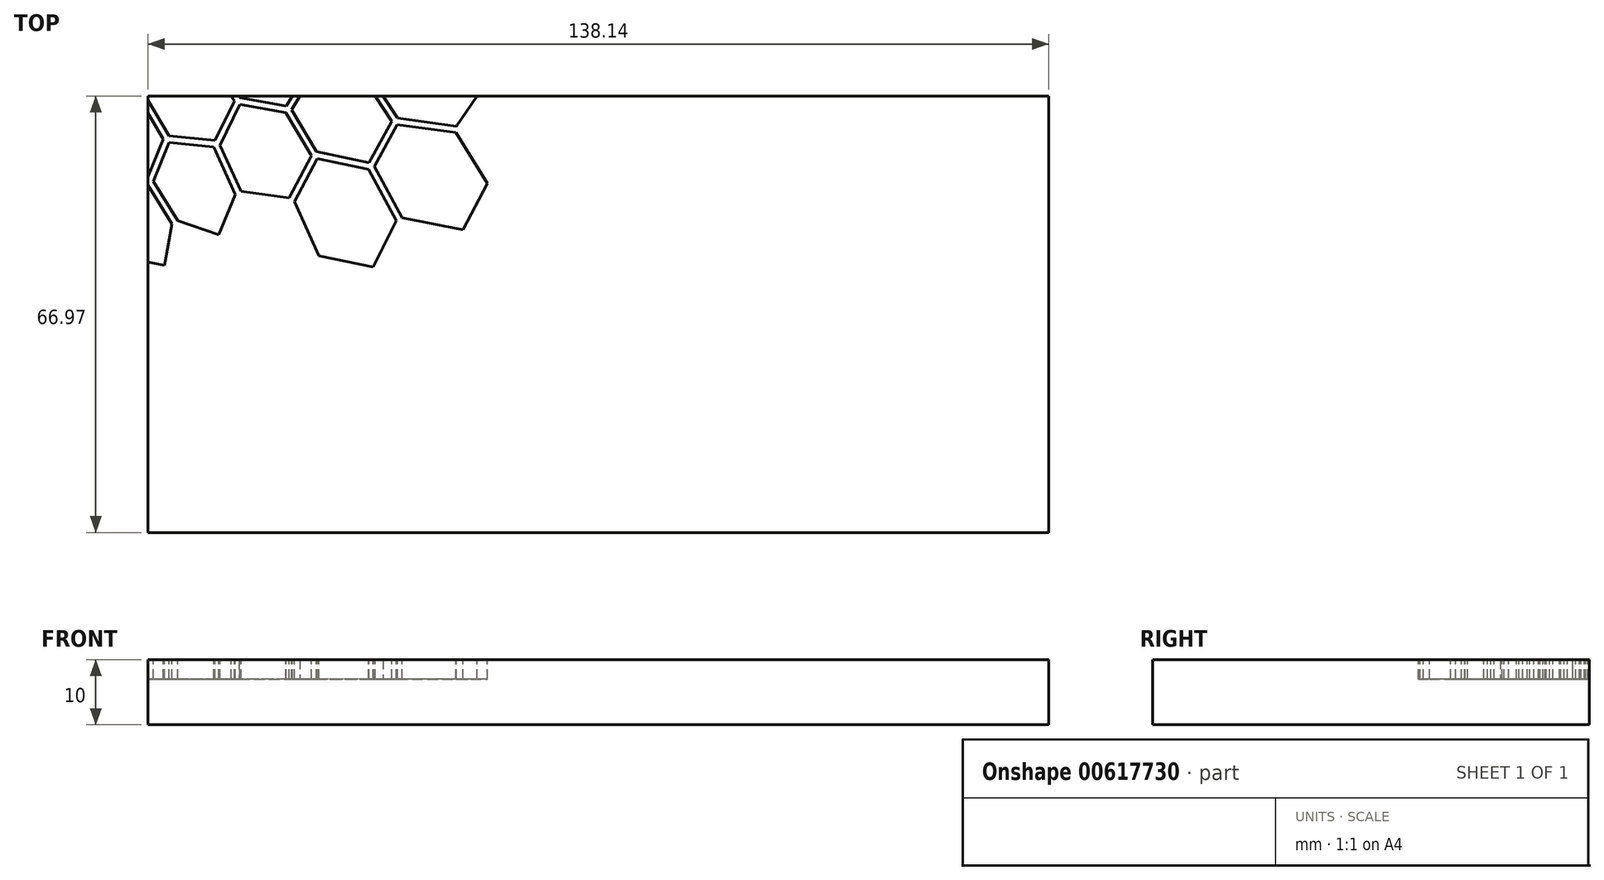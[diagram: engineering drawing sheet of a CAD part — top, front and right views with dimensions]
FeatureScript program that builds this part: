
annotation { "Feature Type Name" : "Feature", "Feature Type Description" : "" }
export const myFeature = defineFeature(function(context is Context, id is Id, definition is map)
    precondition{}
    {
        {
            var Q0;
            Q0=qCreatedBy(makeId("Top.planeOp"),FACE);
            var sketch = newSketch(context, id + "F0", { "sketchPlane" : qUnion([Q0])});
            skLineSegment(sketch, "E0.bottom", {"start": v(-69.07, 33.48) * mm, "end": v(69.07, 33.48) * mm});
            skLineSegment(sketch, "E0.top", {"start": v(-69.07, -33.48) * mm, "end": v(69.07, -33.48) * mm});
            skLineSegment(sketch, "E0.left", {"start": v(-69.07, 33.48) * mm, "end": v(-69.07, -33.48) * mm});
            skLineSegment(sketch, "E0.right", {"start": v(69.07, 33.48) * mm, "end": v(69.07, -33.48) * mm});
            skPoint(sketch, "E0.middle", {"position": v(0, 0) * mm});
            skSolve(sketch);
        }
        {
            var Q0;
            Q0=makeQuery(id+"F0.imprint","IMPRINT",FACE,{"disambiguationData":[TD([[makeQuery(id+"F0.imprint","IMPRINT",EDGE,{"derivedFrom":sQuery(id+"F0.wireOp",EDGE,"E0.bottom")}),-1.0]])]});
            extrude(context, id + "F1", {"entities" : qUnion([Q0]), "depth" : 10 * mm, "offsetDistance" : 25 * mm});
        }
        {
            var Q0;
            Q0=makeQuery(id+"F1.opExtrude","CAP_FACE",FACE,{"disambiguationData":[OSD([sQuery(id+"F0.wireOp",EDGE,"E0.bottom"),sQuery(id+"F0.wireOp",EDGE,"E0.top"),sQuery(id+"F0.wireOp",EDGE,"E0.left"),sQuery(id+"F0.wireOp",EDGE,"E0.right")])],"isStart":false});
            var sketch = newSketch(context, id + "F2", { "sketchPlane" : qUnion([Q0])});
            skLineSegment(sketch, "E1", {"start": v(-96.9, 29.49) * mm, "end": v(-94.4, 29.51) * mm});
            skLineSegment(sketch, "E2", {"start": v(-94.4, 29.51) * mm, "end": v(-91.05, 23.93) * mm});
            skLineSegment(sketch, "E3", {"start": v(-91.05, 23.93) * mm, "end": v(-89.26, 18.9) * mm});
            skLineSegment(sketch, "E4", {"start": v(-89.26, 18.9) * mm, "end": v(-92.48, 18.87) * mm});
            skLineSegment(sketch, "E5", {"start": v(-92.48, 18.87) * mm, "end": v(-96.9, 29.49) * mm});
            skLineSegment(sketch, "E6", {"start": v(-99.77, 40.38) * mm, "end": v(-98.18, 44.72) * mm});
            skLineSegment(sketch, "E7", {"start": v(-98.18, 44.72) * mm, "end": v(-92.33, 44.3) * mm});
            skLineSegment(sketch, "E8", {"start": v(-92.33, 44.3) * mm, "end": v(-88.21, 39.6) * mm});
            skLineSegment(sketch, "E9", {"start": v(-88.21, 39.6) * mm, "end": v(-90.25, 35.15) * mm});
            skLineSegment(sketch, "E10", {"start": v(-90.25, 35.15) * mm, "end": v(-95.03, 36.47) * mm});
            skLineSegment(sketch, "E11", {"start": v(-95.03, 36.47) * mm, "end": v(-95.02, 36.49) * mm});
            skLineSegment(sketch, "E12", {"start": v(-95.02, 36.49) * mm, "end": v(-99.77, 40.38) * mm});
            skLineSegment(sketch, "E13", {"start": v(-69.46, 44.58) * mm, "end": v(-66.16, 48.77) * mm});
            skLineSegment(sketch, "E14", {"start": v(-66.16, 48.77) * mm, "end": v(-59.5, 48.5) * mm});
            skLineSegment(sketch, "E15", {"start": v(-59.5, 48.5) * mm, "end": v(-55.92, 44.1) * mm});
            skLineSegment(sketch, "E16", {"start": v(-55.92, 44.1) * mm, "end": v(-59.15, 39.22) * mm});
            skLineSegment(sketch, "E17", {"start": v(-59.15, 39.22) * mm, "end": v(-66.18, 39.89) * mm});
            skLineSegment(sketch, "E18", {"start": v(-66.18, 39.89) * mm, "end": v(-69.46, 44.58) * mm});
            skLineSegment(sketch, "E19", {"start": v(-66.97, 39.28) * mm, "end": v(-70.08, 34.05) * mm});
            skLineSegment(sketch, "E20", {"start": v(-70.08, 34.05) * mm, "end": v(-76.45, 34.25) * mm});
            skLineSegment(sketch, "E21", {"start": v(-76.45, 34.25) * mm, "end": v(-79.94, 39.65) * mm});
            skLineSegment(sketch, "E22", {"start": v(-79.94, 39.65) * mm, "end": v(-76.78, 44.28) * mm});
            skLineSegment(sketch, "E23", {"start": v(-76.78, 44.28) * mm, "end": v(-70.4, 44.19) * mm});
            skLineSegment(sketch, "E24", {"start": v(-70.4, 44.19) * mm, "end": v(-66.97, 39.28) * mm});
            skLineSegment(sketch, "E25", {"start": v(-58.56, 48.95) * mm, "end": v(-54.4, 52.87) * mm});
            skLineSegment(sketch, "E26", {"start": v(-54.4, 52.87) * mm, "end": v(-47.4, 52.87) * mm});
            skLineSegment(sketch, "E27", {"start": v(-47.4, 52.87) * mm, "end": v(-44.1, 48.73) * mm});
            skLineSegment(sketch, "E28", {"start": v(-44.1, 48.73) * mm, "end": v(-48.04, 43.8) * mm});
            skLineSegment(sketch, "E29", {"start": v(-48.04, 43.8) * mm, "end": v(-54.95, 44.5) * mm});
            skLineSegment(sketch, "E30", {"start": v(-54.95, 44.5) * mm, "end": v(-58.56, 48.95) * mm});
            skLineSegment(sketch, "E31", {"start": v(-59.43, 49.5) * mm, "end": v(-66.16, 49.77) * mm});
            skLineSegment(sketch, "E32", {"start": v(-66.16, 49.77) * mm, "end": v(-69.16, 53.28) * mm});
            skLineSegment(sketch, "E33", {"start": v(-69.16, 53.28) * mm, "end": v(-64.88, 56.37) * mm});
            skLineSegment(sketch, "E34", {"start": v(-64.88, 56.37) * mm, "end": v(-58.33, 56.82) * mm});
            skLineSegment(sketch, "E35", {"start": v(-58.33, 56.82) * mm, "end": v(-55.29, 53.4) * mm});
            skLineSegment(sketch, "E36", {"start": v(-55.29, 53.4) * mm, "end": v(-59.43, 49.5) * mm});
            skLineSegment(sketch, "E37", {"start": v(-67.04, 49.26) * mm, "end": v(-70.25, 45.19) * mm});
            skLineSegment(sketch, "E38", {"start": v(-70.25, 45.19) * mm, "end": v(-76.82, 45.28) * mm});
            skLineSegment(sketch, "E39", {"start": v(-76.82, 45.28) * mm, "end": v(-80.27, 49.12) * mm});
            skLineSegment(sketch, "E40", {"start": v(-80.27, 49.12) * mm, "end": v(-77.02, 52.71) * mm});
            skLineSegment(sketch, "E41", {"start": v(-77.02, 52.71) * mm, "end": v(-70.12, 52.86) * mm});
            skLineSegment(sketch, "E42", {"start": v(-70.12, 52.86) * mm, "end": v(-67.04, 49.26) * mm});
            skLineSegment(sketch, "E43", {"start": v(-77.68, 44.74) * mm, "end": v(-80.8, 40.16) * mm});
            skLineSegment(sketch, "E44", {"start": v(-80.8, 40.16) * mm, "end": v(-87.4, 40.2) * mm});
            skLineSegment(sketch, "E45", {"start": v(-87.4, 40.2) * mm, "end": v(-91.4, 44.76) * mm});
            skLineSegment(sketch, "E46", {"start": v(-91.4, 44.76) * mm, "end": v(-87.63, 48.53) * mm});
            skLineSegment(sketch, "E47", {"start": v(-87.63, 48.53) * mm, "end": v(-81.16, 48.62) * mm});
            skLineSegment(sketch, "E48", {"start": v(-81.16, 48.62) * mm, "end": v(-77.68, 44.74) * mm});
            skLineSegment(sketch, "E49", {"start": v(-87.3, 39.2) * mm, "end": v(-80.81, 39.16) * mm});
            skLineSegment(sketch, "E50", {"start": v(-80.81, 39.16) * mm, "end": v(-77.3, 33.73) * mm});
            skLineSegment(sketch, "E51", {"start": v(-77.3, 33.73) * mm, "end": v(-79.8, 28.65) * mm});
            skLineSegment(sketch, "E52", {"start": v(-79.8, 28.65) * mm, "end": v(-85.06, 30.3) * mm});
            skLineSegment(sketch, "E53", {"start": v(-85.06, 30.3) * mm, "end": v(-89.38, 34.63) * mm});
            skLineSegment(sketch, "E54", {"start": v(-89.38, 34.63) * mm, "end": v(-87.3, 39.2) * mm});
            skLineSegment(sketch, "E55", {"start": v(-76.42, 33.25) * mm, "end": v(-70.3, 33.06) * mm});
            skLineSegment(sketch, "E56", {"start": v(-70.3, 33.06) * mm, "end": v(-70.32, 33.04) * mm});
            skLineSegment(sketch, "E57", {"start": v(-70.32, 33.04) * mm, "end": v(-66.73, 26.85) * mm});
            skLineSegment(sketch, "E58", {"start": v(-66.73, 26.85) * mm, "end": v(-69.11, 21) * mm});
            skLineSegment(sketch, "E59", {"start": v(-69.11, 21) * mm, "end": v(-75.18, 23.2) * mm});
            skLineSegment(sketch, "E60", {"start": v(-75.18, 23.2) * mm, "end": v(-78.95, 28.1) * mm});
            skLineSegment(sketch, "E61", {"start": v(-78.95, 28.1) * mm, "end": v(-76.42, 33.25) * mm});
            skLineSegment(sketch, "E62", {"start": v(-69.34, 33.33) * mm, "end": v(-66.05, 38.87) * mm});
            skLineSegment(sketch, "E63", {"start": v(-66.05, 38.87) * mm, "end": v(-59.34, 38.23) * mm});
            skLineSegment(sketch, "E64", {"start": v(-59.34, 38.23) * mm, "end": v(-55.82, 32.73) * mm});
            skLineSegment(sketch, "E65", {"start": v(-55.82, 32.73) * mm, "end": v(-58.8, 26.67) * mm});
            skLineSegment(sketch, "E66", {"start": v(-58.8, 26.67) * mm, "end": v(-65.87, 27.36) * mm});
            skLineSegment(sketch, "E67", {"start": v(-65.87, 27.36) * mm, "end": v(-69.34, 33.33) * mm});
            skLineSegment(sketch, "E68", {"start": v(-58.37, 38.58) * mm, "end": v(-55.12, 43.5) * mm});
            skLineSegment(sketch, "E69", {"start": v(-55.12, 43.5) * mm, "end": v(-48.1, 42.8) * mm});
            skLineSegment(sketch, "E70", {"start": v(-48.1, 42.8) * mm, "end": v(-44.57, 37.52) * mm});
            skLineSegment(sketch, "E71", {"start": v(-44.57, 37.52) * mm, "end": v(-47.85, 31.94) * mm});
            skLineSegment(sketch, "E72", {"start": v(-47.85, 31.94) * mm, "end": v(-54.94, 33.21) * mm});
            skLineSegment(sketch, "E73", {"start": v(-54.94, 33.21) * mm, "end": v(-58.37, 38.58) * mm});
            skLineSegment(sketch, "E74", {"start": v(-43.71, 37) * mm, "end": v(-35.9, 36.1) * mm});
            skLineSegment(sketch, "E75", {"start": v(-35.9, 36.1) * mm, "end": v(-31.7, 29.62) * mm});
            skLineSegment(sketch, "E76", {"start": v(-31.7, 29.62) * mm, "end": v(-35.18, 23.27) * mm});
            skLineSegment(sketch, "E77", {"start": v(-35.18, 23.27) * mm, "end": v(-43.22, 24.96) * mm});
            skLineSegment(sketch, "E78", {"start": v(-43.22, 24.96) * mm, "end": v(-47.02, 31.39) * mm});
            skLineSegment(sketch, "E79", {"start": v(-47.02, 31.39) * mm, "end": v(-43.71, 37) * mm});
            skLineSegment(sketch, "E80", {"start": v(-43.7, 38) * mm, "end": v(-47.2, 43.26) * mm});
            skLineSegment(sketch, "E81", {"start": v(-47.2, 43.26) * mm, "end": v(-43.32, 48.12) * mm});
            skLineSegment(sketch, "E82", {"start": v(-43.32, 48.12) * mm, "end": v(-35.45, 47.73) * mm});
            skLineSegment(sketch, "E83", {"start": v(-35.45, 47.73) * mm, "end": v(-31.53, 42.69) * mm});
            skLineSegment(sketch, "E84", {"start": v(-31.53, 42.69) * mm, "end": v(-35.83, 37.1) * mm});
            skLineSegment(sketch, "E85", {"start": v(-35.83, 37.1) * mm, "end": v(-43.7, 38) * mm});
            skLineSegment(sketch, "E86", {"start": v(-35.61, 48.74) * mm, "end": v(-43.13, 49.1) * mm});
            skLineSegment(sketch, "E87", {"start": v(-43.13, 49.1) * mm, "end": v(-46.48, 53.31) * mm});
            skLineSegment(sketch, "E88", {"start": v(-46.48, 53.31) * mm, "end": v(-42.12, 57.34) * mm});
            skLineSegment(sketch, "E89", {"start": v(-42.12, 57.34) * mm, "end": v(-34.51, 57.6) * mm});
            skLineSegment(sketch, "E90", {"start": v(-34.51, 57.6) * mm, "end": v(-31, 53.74) * mm});
            skLineSegment(sketch, "E91", {"start": v(-31, 53.74) * mm, "end": v(-35.61, 48.74) * mm});
            skLineSegment(sketch, "E92", {"start": v(-47.36, 53.87) * mm, "end": v(-54.37, 53.87) * mm});
            skLineSegment(sketch, "E93", {"start": v(-54.37, 53.87) * mm, "end": v(-57.38, 57.25) * mm});
            skLineSegment(sketch, "E94", {"start": v(-57.38, 57.25) * mm, "end": v(-52.98, 60.47) * mm});
            skLineSegment(sketch, "E95", {"start": v(-52.98, 60.47) * mm, "end": v(-45.92, 60.97) * mm});
            skLineSegment(sketch, "E96", {"start": v(-45.92, 60.97) * mm, "end": v(-42.97, 57.91) * mm});
            skLineSegment(sketch, "E97", {"start": v(-42.97, 57.91) * mm, "end": v(-47.36, 53.87) * mm});
            skLineSegment(sketch, "E98", {"start": v(-58.3, 57.82) * mm, "end": v(-64.77, 57.38) * mm});
            skLineSegment(sketch, "E99", {"start": v(-64.77, 57.38) * mm, "end": v(-67.5, 59.64) * mm});
            skLineSegment(sketch, "E100", {"start": v(-67.5, 59.64) * mm, "end": v(-63.01, 61.94) * mm});
            skLineSegment(sketch, "E101", {"start": v(-63.01, 61.94) * mm, "end": v(-56.31, 63.25) * mm});
            skLineSegment(sketch, "E102", {"start": v(-56.31, 63.25) * mm, "end": v(-53.94, 61) * mm});
            skLineSegment(sketch, "E103", {"start": v(-53.94, 61) * mm, "end": v(-58.3, 57.82) * mm});
            skLineSegment(sketch, "E104", {"start": v(-65.8, 56.94) * mm, "end": v(-70.06, 53.86) * mm});
            skLineSegment(sketch, "E105", {"start": v(-70.06, 53.86) * mm, "end": v(-76.91, 53.71) * mm});
            skLineSegment(sketch, "E106", {"start": v(-76.91, 53.71) * mm, "end": v(-79.73, 55.81) * mm});
            skLineSegment(sketch, "E107", {"start": v(-79.73, 55.81) * mm, "end": v(-75.36, 57.7) * mm});
            skLineSegment(sketch, "E108", {"start": v(-75.36, 57.7) * mm, "end": v(-68.52, 59.2) * mm});
            skLineSegment(sketch, "E109", {"start": v(-68.52, 59.2) * mm, "end": v(-65.8, 56.94) * mm});
            skLineSegment(sketch, "E110", {"start": v(-75.44, 58.7) * mm, "end": v(-75.62, 58.66) * mm});
            skLineSegment(sketch, "E111", {"start": v(-75.62, 58.66) * mm, "end": v(-80.42, 56.6) * mm});
            skLineSegment(sketch, "E112", {"start": v(-80.42, 56.6) * mm, "end": v(-82.56, 57.31) * mm});
            skLineSegment(sketch, "E113", {"start": v(-82.56, 57.31) * mm, "end": v(-73.84, 60.75) * mm});
            skLineSegment(sketch, "E114", {"start": v(-73.84, 60.75) * mm, "end": v(-75.45, 58.7) * mm});
            skLineSegment(sketch, "E115", {"start": v(-75.45, 58.7) * mm, "end": v(-75.44, 58.7) * mm});
            skLineSegment(sketch, "E116", {"start": v(-77.92, 53.22) * mm, "end": v(-81.17, 49.62) * mm});
            skLineSegment(sketch, "E117", {"start": v(-81.17, 49.62) * mm, "end": v(-87.3, 49.53) * mm});
            skLineSegment(sketch, "E118", {"start": v(-87.3, 49.53) * mm, "end": v(-92.22, 51.7) * mm});
            skLineSegment(sketch, "E119", {"start": v(-92.22, 51.7) * mm, "end": v(-87.4, 53.98) * mm});
            skLineSegment(sketch, "E120", {"start": v(-87.4, 53.98) * mm, "end": v(-80.84, 55.4) * mm});
            skLineSegment(sketch, "E121", {"start": v(-80.84, 55.4) * mm, "end": v(-77.92, 53.22) * mm});
            skLineSegment(sketch, "E122", {"start": v(-88.57, 49) * mm, "end": v(-92.28, 45.3) * mm});
            skLineSegment(sketch, "E123", {"start": v(-92.28, 45.3) * mm, "end": v(-97.5, 45.68) * mm});
            skLineSegment(sketch, "E124", {"start": v(-97.5, 45.68) * mm, "end": v(-93.4, 51.13) * mm});
            skLineSegment(sketch, "E125", {"start": v(-93.4, 51.13) * mm, "end": v(-88.57, 49) * mm});
            skLineSegment(sketch, "E126", {"start": v(-90.29, 34.12) * mm, "end": v(-85.7, 29.53) * mm});
            skLineSegment(sketch, "E127", {"start": v(-85.7, 29.53) * mm, "end": v(-85.86, 24.16) * mm});
            skLineSegment(sketch, "E128", {"start": v(-85.86, 24.16) * mm, "end": v(-90.3, 24.61) * mm});
            skLineSegment(sketch, "E129", {"start": v(-90.3, 24.61) * mm, "end": v(-93.65, 30.2) * mm});
            skLineSegment(sketch, "E130", {"start": v(-93.65, 30.2) * mm, "end": v(-94.69, 35.34) * mm});
            skLineSegment(sketch, "E131", {"start": v(-94.69, 35.34) * mm, "end": v(-90.29, 34.12) * mm});
            skLineSegment(sketch, "E132", {"start": v(-89.82, 7.93) * mm, "end": v(-92.11, 17.87) * mm});
            skLineSegment(sketch, "E133", {"start": v(-92.11, 17.87) * mm, "end": v(-88.91, 17.9) * mm});
            skLineSegment(sketch, "E134", {"start": v(-88.91, 17.9) * mm, "end": v(-86.59, 11.34) * mm});
            skLineSegment(sketch, "E135", {"start": v(-86.59, 11.34) * mm, "end": v(-86.3, 6.56) * mm});
            skLineSegment(sketch, "E136", {"start": v(-86.3, 6.56) * mm, "end": v(-89.82, 7.93) * mm});
            skLineSegment(sketch, "E137", {"start": v(-82.46, 11.14) * mm, "end": v(-85.72, 11.86) * mm});
            skLineSegment(sketch, "E138", {"start": v(-85.72, 11.86) * mm, "end": v(-89.86, 23.57) * mm});
            skLineSegment(sketch, "E139", {"start": v(-89.86, 23.57) * mm, "end": v(-85.69, 23.14) * mm});
            skLineSegment(sketch, "E140", {"start": v(-85.69, 23.14) * mm, "end": v(-82.08, 16.57) * mm});
            skLineSegment(sketch, "E141", {"start": v(-82.08, 16.57) * mm, "end": v(-82.46, 11.14) * mm});
            skLineSegment(sketch, "E142", {"start": v(-76.46, 16.24) * mm, "end": v(-81.24, 17.13) * mm});
            skLineSegment(sketch, "E143", {"start": v(-81.24, 17.13) * mm, "end": v(-84.87, 23.73) * mm});
            skLineSegment(sketch, "E144", {"start": v(-84.87, 23.73) * mm, "end": v(-84.71, 29.15) * mm});
            skLineSegment(sketch, "E145", {"start": v(-84.71, 29.15) * mm, "end": v(-79.84, 27.62) * mm});
            skLineSegment(sketch, "E146", {"start": v(-79.84, 27.62) * mm, "end": v(-75.8, 22.38) * mm});
            skLineSegment(sketch, "E147", {"start": v(-75.8, 22.38) * mm, "end": v(-76.46, 16.24) * mm});
            skLineSegment(sketch, "E148", {"start": v(-66.52, 7.5) * mm, "end": v(-72.25, 8.63) * mm});
            skLineSegment(sketch, "E149", {"start": v(-72.25, 8.63) * mm, "end": v(-75.47, 16.07) * mm});
            skLineSegment(sketch, "E150", {"start": v(-75.47, 16.07) * mm, "end": v(-74.83, 22.02) * mm});
            skLineSegment(sketch, "E151", {"start": v(-74.83, 22.02) * mm, "end": v(-69.16, 19.96) * mm});
            skLineSegment(sketch, "E152", {"start": v(-69.16, 19.96) * mm, "end": v(-65.4, 13.84) * mm});
            skLineSegment(sketch, "E153", {"start": v(-65.4, 13.84) * mm, "end": v(-66.52, 7.5) * mm});
            skLineSegment(sketch, "E154", {"start": v(-58.22, 12.19) * mm, "end": v(-64.53, 14.35) * mm});
            skLineSegment(sketch, "E155", {"start": v(-64.53, 14.35) * mm, "end": v(-68.27, 20.41) * mm});
            skLineSegment(sketch, "E156", {"start": v(-68.27, 20.41) * mm, "end": v(-65.85, 26.36) * mm});
            skLineSegment(sketch, "E157", {"start": v(-65.85, 26.36) * mm, "end": v(-59.02, 25.7) * mm});
            skLineSegment(sketch, "E158", {"start": v(-59.02, 25.7) * mm, "end": v(-55.7, 18.39) * mm});
            skLineSegment(sketch, "E159", {"start": v(-55.7, 18.39) * mm, "end": v(-58.22, 12.19) * mm});
            skLineSegment(sketch, "E160", {"start": v(-54.81, 18.86) * mm, "end": v(-58.04, 25.95) * mm});
            skLineSegment(sketch, "E161", {"start": v(-58.04, 25.95) * mm, "end": v(-54.97, 32.2) * mm});
            skLineSegment(sketch, "E162", {"start": v(-54.97, 32.2) * mm, "end": v(-47.91, 30.94) * mm});
            skLineSegment(sketch, "E163", {"start": v(-47.91, 30.94) * mm, "end": v(-44.02, 24.35) * mm});
            skLineSegment(sketch, "E164", {"start": v(-44.02, 24.35) * mm, "end": v(-47.41, 17.85) * mm});
            skLineSegment(sketch, "E165", {"start": v(-47.41, 17.85) * mm, "end": v(-54.81, 18.86) * mm});
            skLineSegment(sketch, "E166", {"start": v(-34.52, 7.25) * mm, "end": v(-42.85, 8.97) * mm});
            skLineSegment(sketch, "E167", {"start": v(-42.85, 8.97) * mm, "end": v(-46.58, 17.29) * mm});
            skLineSegment(sketch, "E168", {"start": v(-46.58, 17.29) * mm, "end": v(-43.12, 23.92) * mm});
            skLineSegment(sketch, "E169", {"start": v(-43.12, 23.92) * mm, "end": v(-35.25, 22.27) * mm});
            skLineSegment(sketch, "E170", {"start": v(-35.25, 22.27) * mm, "end": v(-31, 14.4) * mm});
            skLineSegment(sketch, "E171", {"start": v(-31, 14.4) * mm, "end": v(-34.52, 7.25) * mm});
            skLineSegment(sketch, "E172", {"start": v(-17.01, 20.08) * mm, "end": v(-20.79, 12.96) * mm});
            skLineSegment(sketch, "E173", {"start": v(-20.79, 12.96) * mm, "end": v(-30.1, 14.79) * mm});
            skLineSegment(sketch, "E174", {"start": v(-30.1, 14.79) * mm, "end": v(-30.08, 14.8) * mm});
            skLineSegment(sketch, "E175", {"start": v(-30.08, 14.8) * mm, "end": v(-34.35, 22.7) * mm});
            skLineSegment(sketch, "E176", {"start": v(-34.35, 22.7) * mm, "end": v(-30.84, 29.1) * mm});
            skLineSegment(sketch, "E177", {"start": v(-30.84, 29.1) * mm, "end": v(-21.82, 27.87) * mm});
            skLineSegment(sketch, "E178", {"start": v(-21.82, 27.87) * mm, "end": v(-17.01, 20.08) * mm});
            skLineSegment(sketch, "E179", {"start": v(-17.3, 35.36) * mm, "end": v(-21.76, 28.87) * mm});
            skLineSegment(sketch, "E180", {"start": v(-21.76, 28.87) * mm, "end": v(-30.82, 30.1) * mm});
            skLineSegment(sketch, "E181", {"start": v(-30.82, 30.1) * mm, "end": v(-35, 36.54) * mm});
            skLineSegment(sketch, "E182", {"start": v(-35, 36.54) * mm, "end": v(-30.66, 42.18) * mm});
            skLineSegment(sketch, "E183", {"start": v(-30.66, 42.18) * mm, "end": v(-22.1, 41.83) * mm});
            skLineSegment(sketch, "E184", {"start": v(-22.1, 41.83) * mm, "end": v(-17.3, 35.36) * mm});
            skLineSegment(sketch, "E185", {"start": v(-17.43, 48.43) * mm, "end": v(-22.08, 42.83) * mm});
            skLineSegment(sketch, "E186", {"start": v(-22.08, 42.83) * mm, "end": v(-30.64, 43.18) * mm});
            skLineSegment(sketch, "E187", {"start": v(-30.64, 43.18) * mm, "end": v(-34.64, 48.31) * mm});
            skLineSegment(sketch, "E188", {"start": v(-34.64, 48.31) * mm, "end": v(-30.12, 53.24) * mm});
            skLineSegment(sketch, "E189", {"start": v(-30.12, 53.24) * mm, "end": v(-21.7, 53.12) * mm});
            skLineSegment(sketch, "E190", {"start": v(-21.7, 53.12) * mm, "end": v(-17.43, 48.43) * mm});
            skLineSegment(sketch, "E191", {"start": v(-16.96, 59.12) * mm, "end": v(-21.61, 54.12) * mm});
            skLineSegment(sketch, "E192", {"start": v(-21.61, 54.12) * mm, "end": v(-30.1, 54.24) * mm});
            skLineSegment(sketch, "E193", {"start": v(-30.1, 54.24) * mm, "end": v(-33.49, 57.96) * mm});
            skLineSegment(sketch, "E194", {"start": v(-33.49, 57.96) * mm, "end": v(-28.93, 62.22) * mm});
            skLineSegment(sketch, "E195", {"start": v(-28.93, 62.22) * mm, "end": v(-20.57, 63.15) * mm});
            skLineSegment(sketch, "E196", {"start": v(-20.57, 63.15) * mm, "end": v(-16.96, 59.12) * mm});
            skLineSegment(sketch, "E197", {"start": v(-27.07, 69.6) * mm, "end": v(-19.17, 71.15) * mm});
            skLineSegment(sketch, "E198", {"start": v(-19.17, 71.15) * mm, "end": v(-16.73, 68.13) * mm});
            skLineSegment(sketch, "E199", {"start": v(-16.73, 68.13) * mm, "end": v(-20.6, 64.15) * mm});
            skLineSegment(sketch, "E200", {"start": v(-20.6, 64.15) * mm, "end": v(-28.96, 63.23) * mm});
            skLineSegment(sketch, "E201", {"start": v(-28.96, 63.23) * mm, "end": v(-31.83, 66.25) * mm});
            skLineSegment(sketch, "E202", {"start": v(-31.83, 66.25) * mm, "end": v(-27.07, 69.6) * mm});
            skLineSegment(sketch, "E203", {"start": v(-32.86, 65.89) * mm, "end": v(-29.86, 62.72) * mm});
            skLineSegment(sketch, "E204", {"start": v(-29.86, 62.72) * mm, "end": v(-34.25, 58.61) * mm});
            skLineSegment(sketch, "E205", {"start": v(-34.25, 58.61) * mm, "end": v(-42, 58.34) * mm});
            skLineSegment(sketch, "E206", {"start": v(-42, 58.34) * mm, "end": v(-44.97, 61.42) * mm});
            skLineSegment(sketch, "E207", {"start": v(-44.97, 61.42) * mm, "end": v(-40.44, 64.79) * mm});
            skLineSegment(sketch, "E208", {"start": v(-40.44, 64.79) * mm, "end": v(-32.86, 65.89) * mm});
            skLineSegment(sketch, "E209", {"start": v(-43.42, 67.76) * mm, "end": v(-41.25, 65.43) * mm});
            skLineSegment(sketch, "E210", {"start": v(-41.25, 65.43) * mm, "end": v(-45.9, 61.97) * mm});
            skLineSegment(sketch, "E211", {"start": v(-45.9, 61.97) * mm, "end": v(-52.97, 61.47) * mm});
            skLineSegment(sketch, "E212", {"start": v(-52.97, 61.47) * mm, "end": v(-55.3, 63.68) * mm});
            skLineSegment(sketch, "E213", {"start": v(-55.3, 63.68) * mm, "end": v(-50.24, 66.4) * mm});
            skLineSegment(sketch, "E214", {"start": v(-50.24, 66.4) * mm, "end": v(-43.42, 67.76) * mm});
            skLineSegment(sketch, "E215", {"start": v(-60.54, 65.6) * mm, "end": v(-55.72, 68.33) * mm});
            skLineSegment(sketch, "E216", {"start": v(-55.72, 68.33) * mm, "end": v(-50, 69.62) * mm});
            skLineSegment(sketch, "E217", {"start": v(-50, 69.62) * mm, "end": v(-50.82, 67.23) * mm});
            skLineSegment(sketch, "E218", {"start": v(-50.82, 67.23) * mm, "end": v(-56.32, 64.27) * mm});
            skLineSegment(sketch, "E219", {"start": v(-56.32, 64.27) * mm, "end": v(-62.05, 63.15) * mm});
            skLineSegment(sketch, "E220", {"start": v(-62.05, 63.15) * mm, "end": v(-60.54, 65.6) * mm});
            skLineSegment(sketch, "E221", {"start": v(-61.96, 65.2) * mm, "end": v(-63.4, 62.87) * mm});
            skLineSegment(sketch, "E222", {"start": v(-63.4, 62.87) * mm, "end": v(-68.56, 60.2) * mm});
            skLineSegment(sketch, "E223", {"start": v(-68.56, 60.2) * mm, "end": v(-73.91, 59.04) * mm});
            skLineSegment(sketch, "E224", {"start": v(-73.91, 59.04) * mm, "end": v(-71.98, 61.5) * mm});
            skLineSegment(sketch, "E225", {"start": v(-71.98, 61.5) * mm, "end": v(-66.72, 64.08) * mm});
            skLineSegment(sketch, "E226", {"start": v(-66.72, 64.08) * mm, "end": v(-61.96, 65.2) * mm});
            skLineSegment(sketch, "E227", {"start": v(-64.67, 70.78) * mm, "end": v(-60.21, 70.4) * mm});
            skLineSegment(sketch, "E228", {"start": v(-60.21, 70.4) * mm, "end": v(-64.08, 68.19) * mm});
            skLineSegment(sketch, "E229", {"start": v(-64.08, 68.19) * mm, "end": v(-69.91, 66.9) * mm});
            skLineSegment(sketch, "E230", {"start": v(-69.91, 66.9) * mm, "end": v(-64.67, 70.78) * mm});
            skLineSegment(sketch, "E231", {"start": v(-71.96, 65.42) * mm, "end": v(-65.34, 66.89) * mm});
            skLineSegment(sketch, "E232", {"start": v(-65.34, 66.89) * mm, "end": v(-67.05, 65.03) * mm});
            skLineSegment(sketch, "E233", {"start": v(-67.05, 65.03) * mm, "end": v(-67.06, 65.03) * mm});
            skLineSegment(sketch, "E234", {"start": v(-67.06, 65.03) * mm, "end": v(-72.5, 62.35) * mm});
            skLineSegment(sketch, "E235", {"start": v(-72.5, 62.35) * mm, "end": v(-73.5, 61.96) * mm});
            skLineSegment(sketch, "E236", {"start": v(-73.5, 61.96) * mm, "end": v(-78.47, 61.68) * mm});
            skLineSegment(sketch, "E237", {"start": v(-78.47, 61.68) * mm, "end": v(-71.96, 65.42) * mm});
            skLineSegment(sketch, "E238", {"start": v(-86.08, 56.82) * mm, "end": v(-84.4, 56.87) * mm});
            skLineSegment(sketch, "E239", {"start": v(-84.4, 56.87) * mm, "end": v(-82.16, 56.13) * mm});
            skLineSegment(sketch, "E240", {"start": v(-82.16, 56.13) * mm, "end": v(-87.51, 54.98) * mm});
            skLineSegment(sketch, "E241", {"start": v(-87.51, 54.98) * mm, "end": v(-88.64, 55.47) * mm});
            skLineSegment(sketch, "E242", {"start": v(-88.64, 55.47) * mm, "end": v(-86.08, 56.82) * mm});
            skLineSegment(sketch, "E243", {"start": v(-89.76, 54.88) * mm, "end": v(-88.77, 54.44) * mm});
            skLineSegment(sketch, "E244", {"start": v(-88.77, 54.44) * mm, "end": v(-93.14, 52.37) * mm});
            skLineSegment(sketch, "E245", {"start": v(-93.14, 52.37) * mm, "end": v(-93.96, 52.75) * mm});
            skLineSegment(sketch, "E246", {"start": v(-93.96, 52.75) * mm, "end": v(-89.76, 54.88) * mm});
            skLineSegment(sketch, "E247", {"start": v(-98.4, 49.5) * mm, "end": v(-95.05, 52.16) * mm});
            skLineSegment(sketch, "E248", {"start": v(-95.05, 52.16) * mm, "end": v(-94.18, 51.75) * mm});
            skLineSegment(sketch, "E249", {"start": v(-94.18, 51.75) * mm, "end": v(-98.2, 46.4) * mm});
            skLineSegment(sketch, "E250", {"start": v(-98.2, 46.4) * mm, "end": v(-99.51, 47.88) * mm});
            skLineSegment(sketch, "E251", {"start": v(-99.51, 47.88) * mm, "end": v(-98.4, 49.5) * mm});
            skLineSegment(sketch, "E252", {"start": v(-100.95, 44.63) * mm, "end": v(-100, 46.91) * mm});
            skLineSegment(sketch, "E253", {"start": v(-100, 46.91) * mm, "end": v(-98.9, 45.67) * mm});
            skLineSegment(sketch, "E254", {"start": v(-98.9, 45.67) * mm, "end": v(-100.64, 40.92) * mm});
            skLineSegment(sketch, "E255", {"start": v(-100.64, 40.92) * mm, "end": v(-101.69, 40.94) * mm});
            skLineSegment(sketch, "E256", {"start": v(-101.69, 40.94) * mm, "end": v(-100.95, 44.63) * mm});
            skLineSegment(sketch, "E257", {"start": v(-101.72, 39.84) * mm, "end": v(-100.73, 39.88) * mm});
            skLineSegment(sketch, "E258", {"start": v(-100.73, 39.88) * mm, "end": v(-95.8, 35.84) * mm});
            skLineSegment(sketch, "E259", {"start": v(-95.8, 35.84) * mm, "end": v(-94.73, 30.5) * mm});
            skLineSegment(sketch, "E260", {"start": v(-94.73, 30.5) * mm, "end": v(-97.3, 30.48) * mm});
            skLineSegment(sketch, "E261", {"start": v(-97.3, 30.48) * mm, "end": v(-101.4, 36.53) * mm});
            skLineSegment(sketch, "E262", {"start": v(-101.4, 36.53) * mm, "end": v(-101.72, 39.84) * mm});
            skSolve(sketch);
        }
        {
            var Q0;
            Q0 = qSketchRegion(id + "F2", true);
            extrude(context, id + "F3", {"entities" : qUnion([Q0]), "operationType" : NewBodyOperationType.REMOVE, "oppositeDirection" : true, "depth" : 3 * mm, "offsetDistance" : 25 * mm});
        }
    });
